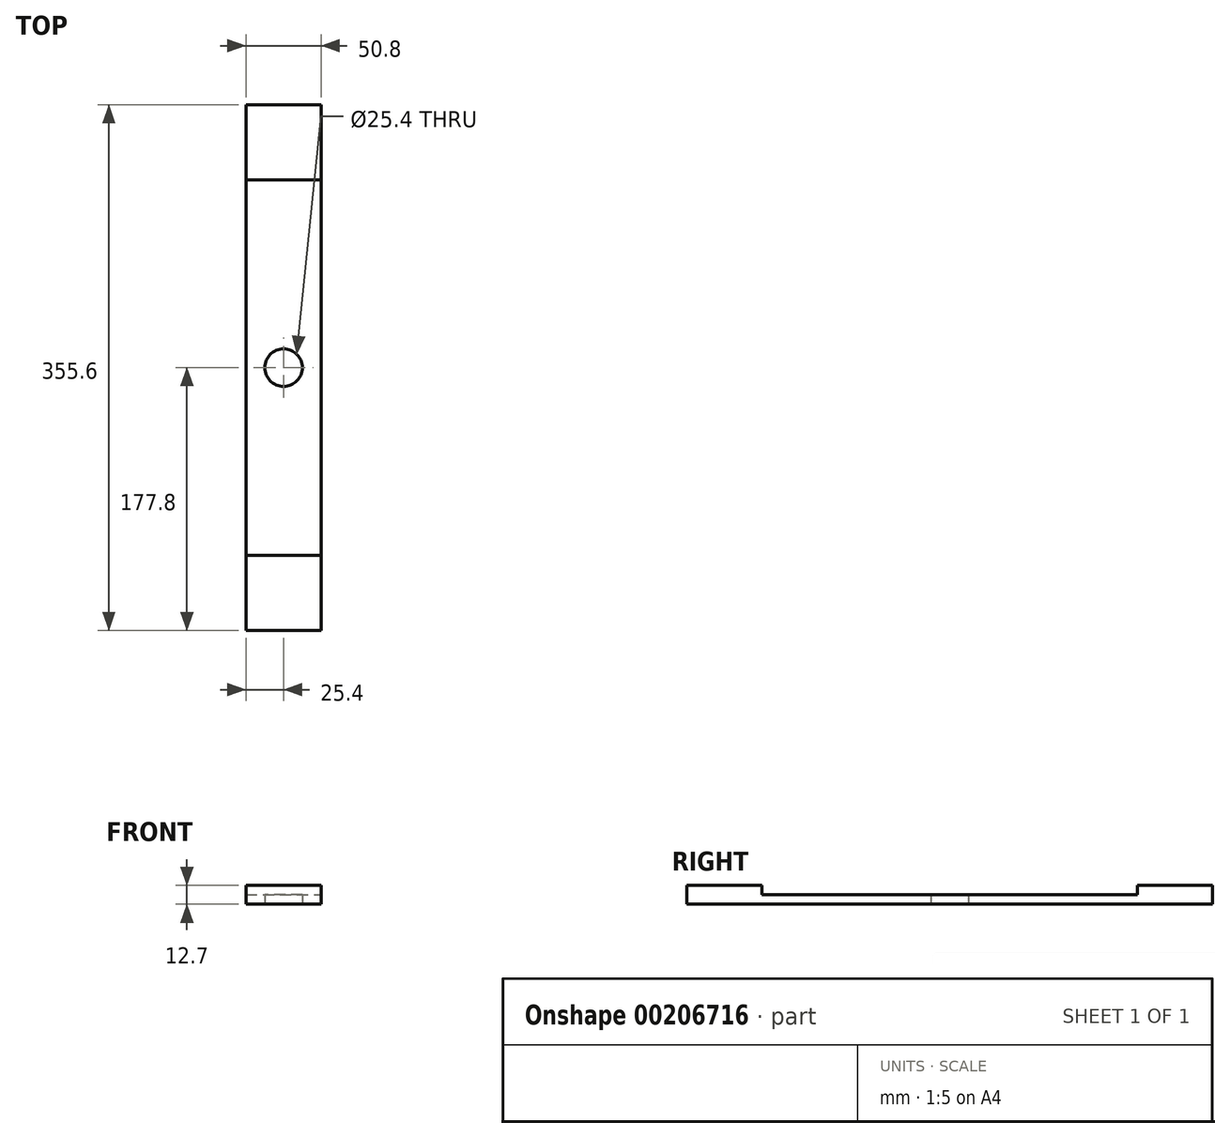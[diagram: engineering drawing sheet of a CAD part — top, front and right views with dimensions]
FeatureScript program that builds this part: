
annotation { "Feature Type Name" : "Feature", "Feature Type Description" : "" }
export const myFeature = defineFeature(function(context is Context, id is Id, definition is map)
    precondition{}
    {
        {
            var Q0;
            Q0=qCreatedBy(makeId("Top.planeOp"),FACE);
            var sketch = newSketch(context, id + "F0", { "sketchPlane" : qUnion([Q0])});
            skLineSegment(sketch, "E0.bottom", {"start": v(25.4, 177.8) * mm, "end": v(-25.4, 177.8) * mm});
            skLineSegment(sketch, "E0.top", {"start": v(25.4, -177.8) * mm, "end": v(-25.4, -177.8) * mm});
            skLineSegment(sketch, "E0.left", {"start": v(25.4, 177.8) * mm, "end": v(25.4, -177.8) * mm});
            skLineSegment(sketch, "E0.right", {"start": v(-25.4, 177.8) * mm, "end": v(-25.4, -177.8) * mm});
            skPoint(sketch, "E0.middle", {"position": v(0, 0) * mm});
            skCircle(sketch, "E1", {"center": v(0, 0) * mm, "radius": 12.7 * mm});
            skSolve(sketch);
        }
        {
            var Q0;
            Q0=makeQuery(id+"F0.imprint","IMPRINT",FACE,{"disambiguationData":[TD([[makeQuery(id+"F0.imprint","IMPRINT",EDGE,{"derivedFrom":sQuery(id+"F0.wireOp",EDGE,"E0.bottom")}),1.0]])]});
            extrude(context, id + "F1", {"entities" : qUnion([Q0]), "depth" : 6.35 * mm});
        }
        {
            var Q0;
            Q0=makeQuery(id+"F1.opExtrude","CAP_FACE",FACE,{"disambiguationData":[OSD([sQuery(id+"F0.wireOp",EDGE,"E0.bottom"),sQuery(id+"F0.wireOp",EDGE,"E0.top"),sQuery(id+"F0.wireOp",EDGE,"E0.left"),sQuery(id+"F0.wireOp",EDGE,"E0.right")])],"isStart":false});
            var sketch = newSketch(context, id + "F2", { "sketchPlane" : qUnion([Q0])});
            skLineSegment(sketch, "E2.bottom", {"start": v(-25.4, -177.8) * mm, "end": v(25.4, -177.8) * mm});
            skLineSegment(sketch, "E2.top", {"start": v(-25.4, -127) * mm, "end": v(25.4, -127) * mm});
            skLineSegment(sketch, "E2.left", {"start": v(-25.4, -177.8) * mm, "end": v(-25.4, -127) * mm});
            skLineSegment(sketch, "E2.right", {"start": v(25.4, -177.8) * mm, "end": v(25.4, -127) * mm});
            skLineSegment(sketch, "E3.bottom", {"start": v(-25.4, 177.8) * mm, "end": v(25.4, 177.8) * mm});
            skLineSegment(sketch, "E3.top", {"start": v(-25.4, 127) * mm, "end": v(25.4, 127) * mm});
            skLineSegment(sketch, "E3.left", {"start": v(-25.4, 177.8) * mm, "end": v(-25.4, 127) * mm});
            skLineSegment(sketch, "E3.right", {"start": v(25.4, 177.8) * mm, "end": v(25.4, 127) * mm});
            skSolve(sketch);
        }
        {
            var Q0;
            Q0=qSketchRegion(id+"F2",true);
            extrude(context, id + "F3", {"entities" : qUnion([Q0]), "operationType" : NewBodyOperationType.ADD, "depth" : 6.35 * mm});
        }
    });
